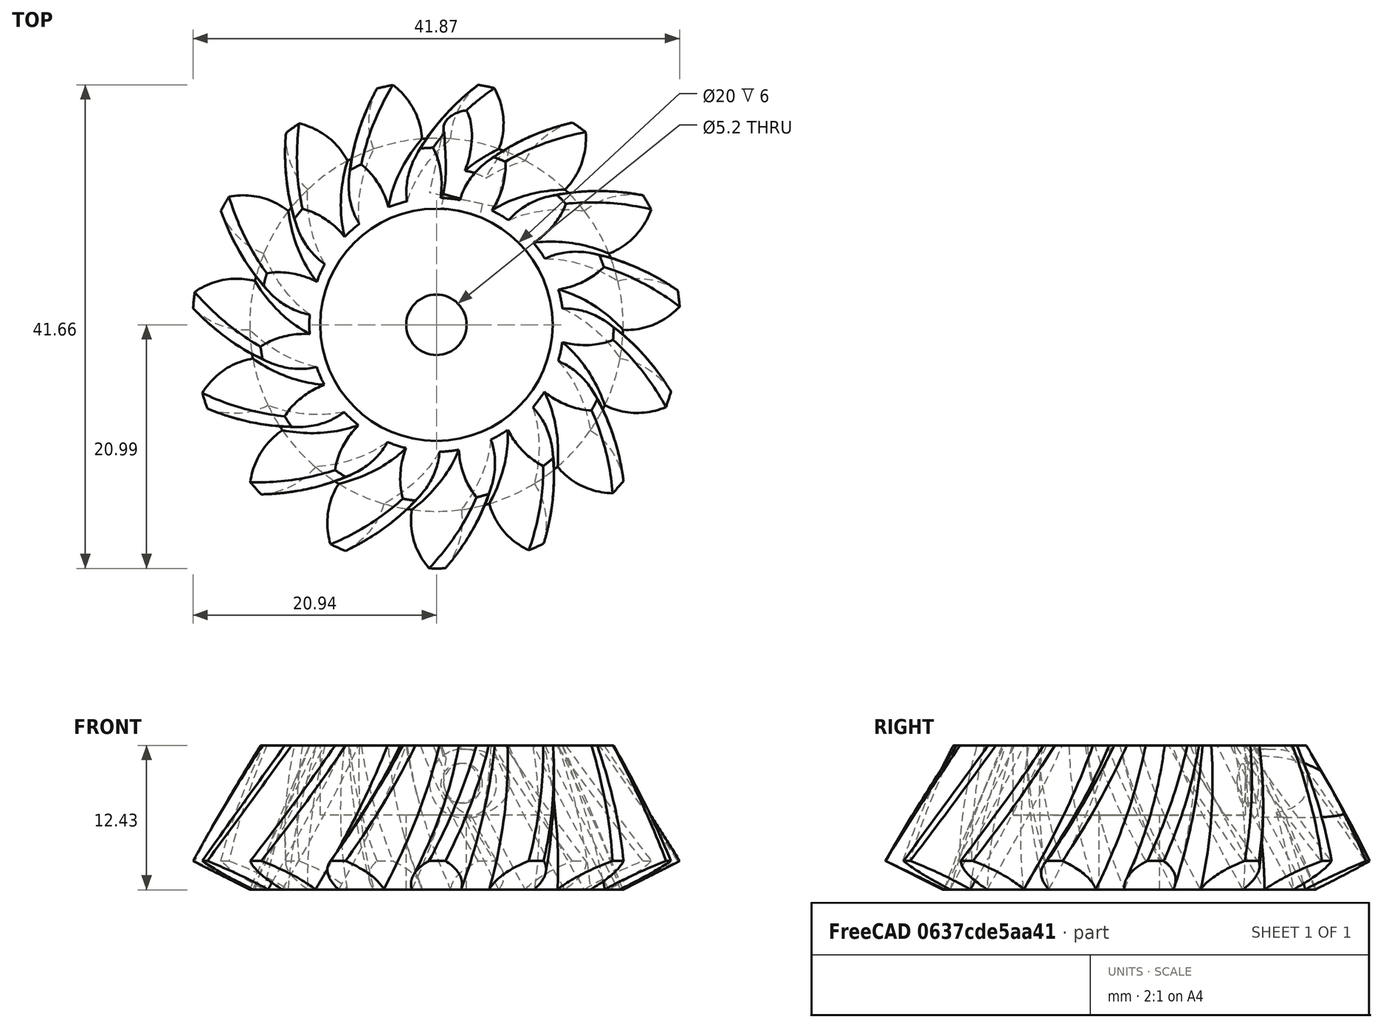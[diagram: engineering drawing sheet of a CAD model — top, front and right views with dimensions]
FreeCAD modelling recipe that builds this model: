
FCSTD DOCUMENT  (FreeCAD 0.16R6460 (Git))
Label: Art56SmallGear
License: All rights reserved
LicenseURL: http://en.wikipedia.org/wiki/All_rights_reserved
objects: Part::Cylinder×5, Part::MultiFuse×2, Part::Feature×1, Part::MultiCommon×1, Part::FeaturePython×1, Part::Cut×1, App::DocumentObjectGroup×1
note: 11 computed .brp shape members not serialized (recipe doc carries the construction recipe); baked Part::Feature solids carry a one-line shape summary decoded from their .brp

FEATURE [Part::Feature] Part__Feature001  label="Bevel Gear"
  Placement = pos=(0,0,38.8416) rot=(0,0,1;0rad)
  shape: bbox 42.05 x 42.1 x 14.15 mm, 92 faces (baked)
FEATURE [Part::Cylinder] Cylinder1033  label="Cylinder1075"
  Angle = 360
  Height = 12.4
  Radius = 27
FEATURE [Part::MultiCommon] Common001
  Shapes = -> [Part__Feature001,Cylinder1033]
FEATURE [Part::Cylinder] Cylinder1034  label="Cylinder1076"
  Angle = 360
  Height = 13
  Radius = 2.6
FEATURE [Part::Cylinder] Cylinder1035  label="Cylinder1077"
  Angle = 360
  Height = 10
  Placement = pos=(0,0,6.4) rot=(0,0,1;0rad)
  Radius = 10
FEATURE [Part::Cylinder] Cylinder1036  label="Cylinder1078"
  Angle = 360
  Height = 10
  Radius = 2.95
FEATURE [Part::Cylinder] Cylinder1037  label="Cylinder1079"
  Angle = 360
  Height = 10
  Placement = pos=(0,0,10) rot=(0,0,1;0rad)
  Radius = 1.7
FEATURE [Part::MultiFuse] Fusion114  label="M3BoltShort"
  Shapes = -> [Cylinder1037,Cylinder1036]
FEATURE [Part::FeaturePython] Clone319  label="Clone of M3BoltShort"  # Draft clone (typed FeaturePython)
  Objects = -> [Fusion114]
  Placement = pos=(4.36615,20.5411,9.15) rot=(0.989133,-0.103962,-0.103962;1.58172rad)
  Scale = (1,1,1)
FEATURE [Part::MultiFuse] Fusion115
  Shapes = -> [Cylinder1034,Cylinder1035,Clone319]
FEATURE [Part::Cut] Cut097  label="Art56SmallGear"
  Base = -> Common001
  Tool = -> Fusion115
FEATURE [App::DocumentObjectGroup] Group  label="Master"
  Group = -> [Fusion114]
